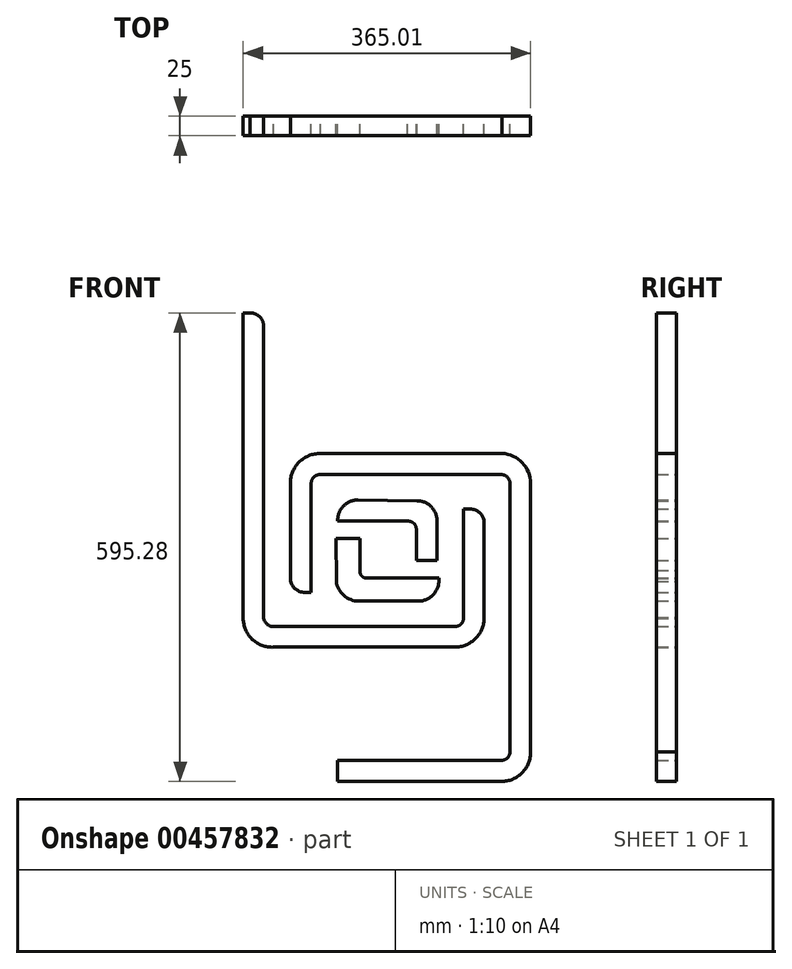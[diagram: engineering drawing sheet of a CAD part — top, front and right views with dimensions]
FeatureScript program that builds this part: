
annotation { "Feature Type Name" : "Feature", "Feature Type Description" : "" }
export const myFeature = defineFeature(function(context is Context, id is Id, definition is map)
    precondition{}
    {
        {
            var Q0;
            Q0=qCreatedBy(makeId("Front.planeOp"),FACE);
            var sketch = newSketch(context, id + "F0", { "sketchPlane" : qUnion([Q0])});
            skLineSegment(sketch, "E0", {"start": v(-182.96, 297.36) * mm, "end": v(-182.96, -90.6) * mm});
            skLineSegment(sketch, "E1", {"start": v(-144.48, -127.35) * mm, "end": v(85.84, -127.35) * mm});
            skLineSegment(sketch, "E2", {"start": v(85.84, -101.2) * mm, "end": v(-144.16, -101.2) * mm});
            skLineSegment(sketch, "E3", {"start": v(-174.48, 297.36) * mm, "end": v(-182.96, 297.36) * mm});
            skLineSegment(sketch, "E4", {"start": v(-156.95, -90.73) * mm, "end": v(-156.95, 280.2) * mm});
            skArc(sketch, "E5", {"start": v(-156.95, 280.2) * mm, "mid": v(-162.1, 292.47) * mm, "end": v(-174.48, 297.36) * mm});
            skArc(sketch, "E6", {"start": v(-182.96, -90.6) * mm, "mid": v(-171.58, -117.2) * mm, "end": v(-144.48, -127.35) * mm});
            skArc(sketch, "E7", {"start": v(-144.16, -101.2) * mm, "mid": v(-152.43, -98.25) * mm, "end": v(-156.95, -90.73) * mm});
            skArc(sketch, "E8", {"start": v(85.84, -101.2) * mm, "mid": v(93.87, -97.8) * mm, "end": v(96.98, -89.64) * mm});
            skArc(sketch, "E9", {"start": v(85.84, -127.35) * mm, "mid": v(112.35, -116.28) * mm, "end": v(123.11, -89.64) * mm});
            skLineSegment(sketch, "E10", {"start": v(123.11, -89.64) * mm, "end": v(123.11, 32.65) * mm});
            skLineSegment(sketch, "E11", {"start": v(96.98, -89.64) * mm, "end": v(96.98, 48.15) * mm});
            skLineSegment(sketch, "E12", {"start": v(96.98, 48.15) * mm, "end": v(105.51, 48.15) * mm});
            skArc(sketch, "E13", {"start": v(105.51, 48.15) * mm, "mid": v(117.24, 43.73) * mm, "end": v(123.11, 32.65) * mm});
            skSolve(sketch);
        }
        {
            var Q0;
            Q0=makeQuery(id+"F0.imprint","IMPRINT",FACE,{"disambiguationData":[TD([[makeQuery(id+"F0.imprint","IMPRINT",EDGE,{"derivedFrom":sQuery(id+"F0.wireOp",EDGE,"E0")}),1.0]])]});
            extrude(context, id + "F1", {"entities" : qUnion([Q0]), "depth" : 25 * mm});
        }
        {
            var Q0;
            Q0=qCreatedBy(makeId("Front.planeOp"),FACE);
            var sketch = newSketch(context, id + "F2", { "sketchPlane" : qUnion([Q0])});
            skLineSegment(sketch, "E14", {"start": v(-64.81, 10.47) * mm, "end": v(-34.72, 10.47) * mm});
            skLineSegment(sketch, "E15", {"start": v(-34.72, 10.47) * mm, "end": v(-34.72, -29.94) * mm});
            skLineSegment(sketch, "E16", {"start": v(-64.81, 10.47) * mm, "end": v(-64.73, -43.75) * mm});
            skLineSegment(sketch, "E17", {"start": v(-26.14, -39.6) * mm, "end": v(65.46, -39.6) * mm});
            skArc(sketch, "E18", {"start": v(-35.98, -68.91) * mm, "mid": v(-55.09, -61.73) * mm, "end": v(-64.73, -43.75) * mm});
            skArc(sketch, "E19", {"start": v(-26.14, -39.6) * mm, "mid": v(-32.6, -36.7) * mm, "end": v(-34.72, -29.94) * mm});
            skLineSegment(sketch, "E20", {"start": v(39.37, -68.91) * mm, "end": v(-35.98, -68.91) * mm});
            skArc(sketch, "E21", {"start": v(39.37, -68.91) * mm, "mid": v(58.98, -60.11) * mm, "end": v(65.46, -39.6) * mm});
            skSolve(sketch);
        }
        {
            var Q0;
            Q0=makeQuery(id+"F2.imprint","IMPRINT",FACE,{"disambiguationData":[TD([[makeQuery(id+"F2.imprint","IMPRINT",EDGE,{"derivedFrom":sQuery(id+"F2.wireOp",EDGE,"E14")}),-1.0]])]});
            extrude(context, id + "F3", {"entities" : qUnion([Q0]), "depth" : 25 * mm});
        }
        {
            var Q0;
            Q0=qCreatedBy(makeId("Front.planeOp"),FACE);
            var sketch = newSketch(context, id + "F4", { "sketchPlane" : qUnion([Q0])});
            skLineSegment(sketch, "E22", {"start": v(-62.92, 32.72) * mm, "end": v(25.71, 32.72) * mm});
            skLineSegment(sketch, "E23", {"start": v(36.9, -16.95) * mm, "end": v(63.15, -16.95) * mm});
            skLineSegment(sketch, "E24", {"start": v(63.15, -16.95) * mm, "end": v(63.15, 33.25) * mm});
            skLineSegment(sketch, "E25", {"start": v(37.55, 58.7) * mm, "end": v(-37.16, 59.63) * mm});
            skArc(sketch, "E26", {"start": v(-37.16, 59.63) * mm, "mid": v(-55.89, 51.77) * mm, "end": v(-62.92, 32.72) * mm});
            skArc(sketch, "E27", {"start": v(63.15, 33.25) * mm, "mid": v(55.64, 51.3) * mm, "end": v(37.55, 58.7) * mm});
            skLineSegment(sketch, "E28", {"start": v(36.9, 22.45) * mm, "end": v(36.9, -16.95) * mm});
            skArc(sketch, "E29", {"start": v(36.9, 22.45) * mm, "mid": v(33.56, 30.05) * mm, "end": v(25.71, 32.72) * mm});
            skSolve(sketch);
        }
        {
            var Q0;
            Q0=makeQuery(id+"F4.imprint","IMPRINT",FACE,{"disambiguationData":[TD([[makeQuery(id+"F4.imprint","IMPRINT",EDGE,{"derivedFrom":sQuery(id+"F4.wireOp",EDGE,"E22")}),1.0]])]});
            extrude(context, id + "F5", {"entities" : qUnion([Q0]), "depth" : 25 * mm});
        }
        {
            var Q0;
            Q0=qCreatedBy(makeId("Front.planeOp"),FACE);
            var sketch = newSketch(context, id + "F6", { "sketchPlane" : qUnion([Q0])});
            skLineSegment(sketch, "E30", {"start": v(-96.6, -57.7) * mm, "end": v(-96.6, 80.64) * mm});
            skLineSegment(sketch, "E31", {"start": v(-63.4, -271.07) * mm, "end": v(-63.4, -297.92) * mm});
            skLineSegment(sketch, "E32", {"start": v(-63.4, -297.92) * mm, "end": v(144.92, -297.92) * mm});
            skLineSegment(sketch, "E33", {"start": v(-104.8, -57.7) * mm, "end": v(-96.6, -57.7) * mm});
            skPoint(sketch, "E34.end.orphan", {"position": v(-123.2, -57.7) * mm});
            skArc(sketch, "E35", {"start": v(-104.8, -57.7) * mm, "mid": v(-117.64, -52.49) * mm, "end": v(-123.2, -39.8) * mm});
            skLineSegment(sketch, "E36", {"start": v(-85.01, 91.98) * mm, "end": v(145.1, 91.98) * mm});
            skLineSegment(sketch, "E37", {"start": v(-123.2, 80.73) * mm, "end": v(-123.2, -39.8) * mm});
            skArc(sketch, "E38", {"start": v(-96.6, 80.64) * mm, "mid": v(-93.19, 88.74) * mm, "end": v(-85.01, 91.98) * mm});
            skArc(sketch, "E39", {"start": v(-123.2, 80.73) * mm, "mid": v(-112, 107.67) * mm, "end": v(-85.01, 118.75) * mm});
            skLineSegment(sketch, "E40", {"start": v(155.89, 80.64) * mm, "end": v(155.89, -259.34) * mm});
            skLineSegment(sketch, "E41", {"start": v(145.91, 118.75) * mm, "end": v(-85.01, 118.75) * mm});
            skArc(sketch, "E42", {"start": v(155.89, 80.64) * mm, "mid": v(152.76, 88.46) * mm, "end": v(145.1, 91.98) * mm});
            skArc(sketch, "E43", {"start": v(182.05, 80.64) * mm, "mid": v(171.58, 106.9) * mm, "end": v(145.91, 118.75) * mm});
            skLineSegment(sketch, "E44", {"start": v(182.05, -260.24) * mm, "end": v(182.05, 80.64) * mm});
            skLineSegment(sketch, "E45", {"start": v(145.1, -271.07) * mm, "end": v(-63.4, -271.07) * mm});
            skArc(sketch, "E46", {"start": v(145.1, -271.07) * mm, "mid": v(153.07, -267.57) * mm, "end": v(155.89, -259.34) * mm});
            skArc(sketch, "E47", {"start": v(144.92, -297.92) * mm, "mid": v(171.37, -286.85) * mm, "end": v(182.05, -260.24) * mm});
            skSolve(sketch);
        }
        {
            var Q0;
            Q0=makeQuery(id+"F6.imprint","IMPRINT",FACE,{"disambiguationData":[TD([[makeQuery(id+"F6.imprint","IMPRINT",EDGE,{"derivedFrom":sQuery(id+"F6.wireOp",EDGE,"E30")}),1.0]])]});
            extrude(context, id + "F7", {"entities" : qUnion([Q0]), "depth" : 25 * mm});
        }
    });
